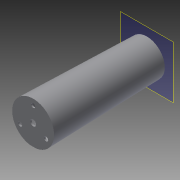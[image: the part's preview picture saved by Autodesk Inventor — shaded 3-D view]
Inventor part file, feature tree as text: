
AUTODESK INVENTOR PART (.ipt)
format: ipt  version: 2014 (Build 180170000, 170)  size: 269,824 bytes
history: native  units: mm
features: sketch x8, extrude x6, other x2, loft x1, shell x1, fillet x1, projected_geometry x1
ambient origin geometry x8: Origin, YZ Plane, XZ Plane, XY Plane, X Axis, Y Axis, Z Axis, Center Point
bodies: Body1 (feature_tree)
feature tree (20):
  other  "ソリッド1"
  sketch  "スケッチ1"
  other  "作業平面1"
  loft  "ロフト1"
  shell  "シェル1"  Thickness=95.0mm
  extrude  "押し出し3"  Depth=30.0mm
  extrude  "押し出し7"  TaperAngle=0.0deg  [1 undecoded]
  extrude  "押し出し12"  TaperAngle=0.0deg  [1 undecoded]
  fillet  "フィレット2"  Radius=1.3mm
  extrude  "押し出し13"  Depth=15.0mm TaperAngle=0.0deg
  extrude  "押し出し14"  Depth=2.6mm
  extrude  "押し出し15"  Depth=10.5mm
  sketch  "スケッチ2"
  sketch  "スケッチ5"
  projected_geometry  "投影ループ1"
  sketch  "スケッチ9"
  sketch  "スケッチ14"
  sketch  "スケッチ15"
  sketch  "スケッチ16"
  sketch  "スケッチ17"
note: 2 required parameter values undecoded (feature->parameter linkage not recoverable at this tier; creation-order binding heuristic only, values carry confidence <= 0.55)
